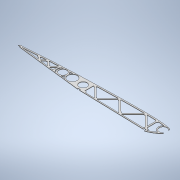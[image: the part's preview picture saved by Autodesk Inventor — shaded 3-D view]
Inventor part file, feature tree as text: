
AUTODESK INVENTOR PART (.ipt)
format: ipt  version: 2022 (Build 260153000, 153)  size: 449,536 bytes
history: native  units: mm
features: extrude x1, sketch x1
ambient origin geometry x8: Origin, YZ Plane, XZ Plane, XY Plane, X Axis, Y Axis, Z Axis, Center Point
bodies: Body1 (feature_tree)
feature tree (2):
  extrude  "Extrusion5"  Depth=1.0mm
  sketch  "Sketch1"  dims[d31=34.456mm d50=368.759386mm d57=16.0mm d69=8.0mm d70=23.0mm d71=8.0mm d73=16.0mm d80=19.0mm d81=16.0mm d82=1.0mm d83=1.0mm d84=1.0mm d85=1.0mm d86=1.0mm d87=0.8mm d88=1.0mm d90=19.0mm d94=5.0mm d95=5.0mm d105=5.0mm d106=5.0mm d108=2.0mm d109=19.0mm d114=5.0mm d115=5.0mm d116=24.0mm d117=2.5mm d118=2.5mm d123=2.5mm d124=2.5mm d125=10.0mm d126=24.0mm d127=24.0mm d128=27.0mm d135=0.5mm d136=45.0deg d139=7.0mm d165=45.0deg d169=27.0mm d175=90.0deg d181=45.0deg d185=7.0mm d186=45.0deg d190=7.0mm d191=45.0deg d197=90.0deg d203=90.0deg d206=7.0mm d207=1.0mm d208=0.0mm]
